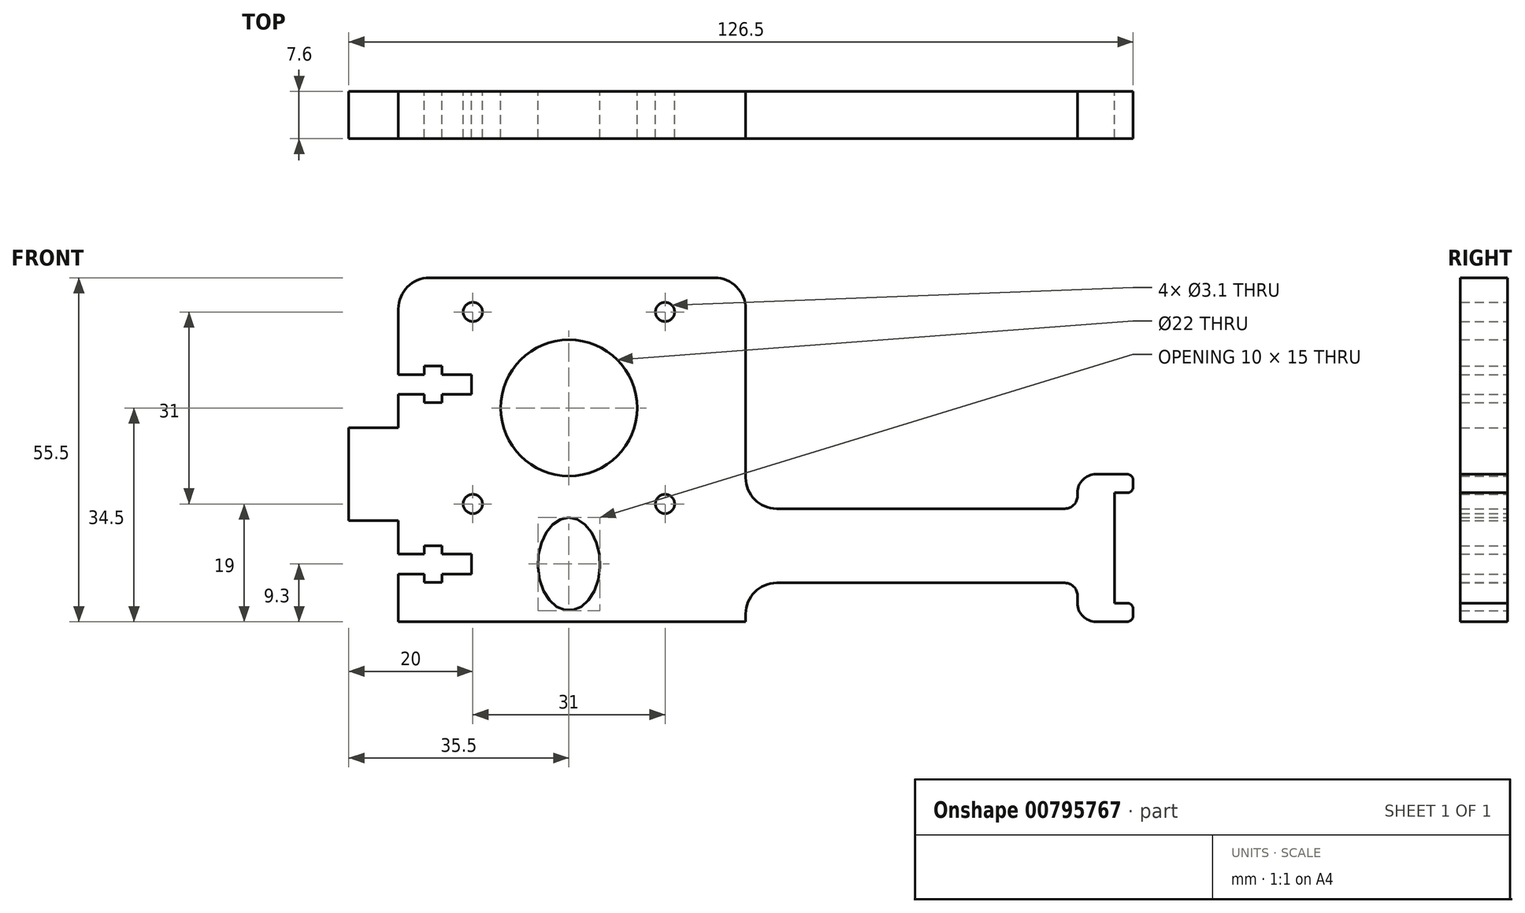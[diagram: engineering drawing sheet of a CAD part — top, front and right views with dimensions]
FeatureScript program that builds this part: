
annotation { "Feature Type Name" : "Feature", "Feature Type Description" : "" }
export const myFeature = defineFeature(function(context is Context, id is Id, definition is map)
    precondition{}
    {
        {
            var Q0;
            Q0=qCreatedBy(makeId("Front.planeOp"),FACE);
            var sketch = newSketch(context, id + "F0", { "sketchPlane" : qUnion([Q0])});
            skLineSegment(sketch, "E0", {"start": v(0, 0) * mm, "end": v(56, 0) * mm});
            skLineSegment(sketch, "E1", {"start": v(56, 0) * mm, "end": v(56, 1.25) * mm});
            skLineSegment(sketch, "E2", {"start": v(61, 6.25) * mm, "end": v(107.5, 6.25) * mm});
            skLineSegment(sketch, "E3", {"start": v(115.5, 3) * mm, "end": v(115.5, 20.8) * mm});
            skLineSegment(sketch, "E4", {"start": v(107.5, 18.25) * mm, "end": v(61, 18.25) * mm});
            skPoint(sketch, "E4.endSnap0", {"position": v(56, 3.12) * mm});
            skLineSegment(sketch, "E5", {"start": v(56, 23.25) * mm, "end": v(56, 50.5) * mm});
            skLineSegment(sketch, "E6", {"start": v(51, 55.5) * mm, "end": v(5, 55.5) * mm});
            skLineSegment(sketch, "E7", {"start": v(0, 50.5) * mm, "end": v(0, 39.9) * mm});
            skLineSegment(sketch, "E8", {"start": v(0, 31.3) * mm, "end": v(-8, 31.3) * mm});
            skLineSegment(sketch, "E9", {"start": v(-8, 31.3) * mm, "end": v(-8, 16.3) * mm});
            skLineSegment(sketch, "E10", {"start": v(-8, 16.3) * mm, "end": v(0, 16.3) * mm});
            skLineSegment(sketch, "E11", {"start": v(0, 16.3) * mm, "end": v(0, 10.9) * mm});
            skCircle(sketch, "E12", {"center": v(27.5, 34.5) * mm, "radius": 11 * mm});
            skCircle(sketch, "E13", {"center": v(43, 50) * mm, "radius": 1.55 * mm});
            skCircle(sketch, "E14.1.0", {"center": v(43, 19) * mm, "radius": 1.55 * mm});
            skCircle(sketch, "E14.2.0", {"center": v(12, 19) * mm, "radius": 1.55 * mm});
            skCircle(sketch, "E14.3.0", {"center": v(12, 50) * mm, "radius": 1.55 * mm});
            skLineSegment(sketch, "E14.anchor1", {"start": v(27.5, 34.5) * mm, "end": v(43, 50) * mm, "construction": true});
            skLineSegment(sketch, "E14.anchor2", {"start": v(27.5, 34.5) * mm, "end": v(12, 50) * mm, "construction": true});
            skLineSegment(sketch, "E15", {"start": v(0, 7.7) * mm, "end": v(4.2, 7.7) * mm});
            skLineSegment(sketch, "E16", {"start": v(4.2, 7.7) * mm, "end": v(4.2, 6.35) * mm});
            skLineSegment(sketch, "E17", {"start": v(7, 6.35) * mm, "end": v(7, 7.7) * mm});
            skLineSegment(sketch, "E18", {"start": v(7, 7.7) * mm, "end": v(11.8, 7.7) * mm});
            skLineSegment(sketch, "E19", {"start": v(11.8, 7.7) * mm, "end": v(11.8, 9.3) * mm});
            skLineSegment(sketch, "E20", {"start": v(7, 6.35) * mm, "end": v(4.2, 6.35) * mm});
            skLineSegment(sketch, "E21", {"start": v(0, 9.3) * mm, "end": v(11.8, 9.3) * mm, "construction": true});
            skLineSegment(sketch, "E22.MirrorCS", {"start": v(11.8, 10.9) * mm, "end": v(11.8, 9.3) * mm});
            skLineSegment(sketch, "E23.MirrorCS", {"start": v(7, 10.9) * mm, "end": v(11.8, 10.9) * mm});
            skLineSegment(sketch, "E24.MirrorCS", {"start": v(7, 12.25) * mm, "end": v(7, 10.9) * mm});
            skLineSegment(sketch, "E25.MirrorCS", {"start": v(7, 12.25) * mm, "end": v(4.2, 12.25) * mm});
            skLineSegment(sketch, "E26.MirrorCS", {"start": v(4.2, 10.9) * mm, "end": v(4.2, 12.25) * mm});
            skEllipse(sketch, "E27", {"center": v(27.5, 9.3) * mm, "majorRadius": 7.5 * mm, "minorRadius": 5 * mm, "majorAxis": v(0, 1)});
            skLineSegment(sketch, "E28", {"start": v(0, 53.5) * mm, "end": v(-8, 53.5) * mm, "construction": true});
            skLineSegment(sketch, "E29", {"start": v(0, 36.7) * mm, "end": v(4.2, 36.7) * mm});
            skLineSegment(sketch, "E30", {"start": v(4.2, 36.7) * mm, "end": v(4.2, 35.35) * mm});
            skLineSegment(sketch, "E31", {"start": v(7, 35.35) * mm, "end": v(7, 36.7) * mm});
            skLineSegment(sketch, "E32", {"start": v(7, 36.7) * mm, "end": v(11.8, 36.7) * mm});
            skLineSegment(sketch, "E33", {"start": v(11.8, 36.7) * mm, "end": v(11.8, 38.3) * mm});
            skLineSegment(sketch, "E34", {"start": v(7, 35.35) * mm, "end": v(4.2, 35.35) * mm});
            skLineSegment(sketch, "E35", {"start": v(0, 38.3) * mm, "end": v(11.8, 38.3) * mm, "construction": true});
            skLineSegment(sketch, "E36.MirrorCS", {"start": v(11.8, 39.9) * mm, "end": v(11.8, 38.3) * mm});
            skLineSegment(sketch, "E37.MirrorCS", {"start": v(7, 39.9) * mm, "end": v(11.8, 39.9) * mm});
            skLineSegment(sketch, "E38.MirrorCS", {"start": v(7, 41.25) * mm, "end": v(7, 39.9) * mm});
            skLineSegment(sketch, "E39.MirrorCS", {"start": v(7, 41.25) * mm, "end": v(4.2, 41.25) * mm});
            skLineSegment(sketch, "E40.MirrorCS", {"start": v(4.2, 39.9) * mm, "end": v(4.2, 41.25) * mm});
            skLineSegment(sketch, "E41", {"start": v(0, 3) * mm, "end": v(-8, 3) * mm, "construction": true});
            skLineSegment(sketch, "E42", {"start": v(-8, 31.3) * mm, "end": v(-8, 53.5) * mm, "construction": true});
            skLineSegment(sketch, "E43", {"start": v(-8, 16.3) * mm, "end": v(-8, 3) * mm, "construction": true});
            skLineSegment(sketch, "E44", {"start": v(-8, 3) * mm, "end": v(-8, 0) * mm, "construction": true});
            skLineSegment(sketch, "E45", {"start": v(-8, 0) * mm, "end": v(0, 0) * mm, "construction": true});
            skLineSegment(sketch, "E46", {"start": v(0, 36.7) * mm, "end": v(0, 31.3) * mm});
            skLineSegment(sketch, "E47", {"start": v(0, 7.7) * mm, "end": v(0, 0) * mm});
            skLineSegment(sketch, "E48", {"start": v(0, 39.9) * mm, "end": v(0, 36.7) * mm, "construction": true});
            skLineSegment(sketch, "E49", {"start": v(0, 10.9) * mm, "end": v(0, 7.7) * mm, "construction": true});
            skLineSegment(sketch, "E50.MirrorCS", {"start": v(0, 39.9) * mm, "end": v(4.2, 39.9) * mm});
            skLineSegment(sketch, "E51.MirrorCS", {"start": v(0, 10.9) * mm, "end": v(4.2, 10.9) * mm});
            skPoint(sketch, "E52.visualSharp", {"position": v(56, 55.5) * mm});
            skArc(sketch, "E52.filletArc", {"start": v(56, 50.5) * mm, "mid": v(54.54, 54.04) * mm, "end": v(51, 55.5) * mm});
            skPoint(sketch, "E53.visualSharp", {"position": v(0, 55.5) * mm});
            skArc(sketch, "E53.filletArc", {"start": v(5, 55.5) * mm, "mid": v(1.46, 54.04) * mm, "end": v(0, 50.5) * mm});
            skPoint(sketch, "E54.visualSharp", {"position": v(56, 18.25) * mm});
            skArc(sketch, "E54.filletArc", {"start": v(56, 23.25) * mm, "mid": v(57.46, 19.71) * mm, "end": v(61, 18.25) * mm});
            skPoint(sketch, "E55.visualSharp", {"position": v(56, 6.25) * mm});
            skArc(sketch, "E55.filletArc", {"start": v(61, 6.25) * mm, "mid": v(57.46, 4.79) * mm, "end": v(56, 1.25) * mm});
            skLineSegment(sketch, "E56", {"start": v(109.5, 4.25) * mm, "end": v(109.5, 3) * mm});
            skLineSegment(sketch, "E57", {"start": v(112.5, 0) * mm, "end": v(117.5, 0) * mm});
            skLineSegment(sketch, "E58", {"start": v(118.5, 1) * mm, "end": v(118.5, 2) * mm});
            skLineSegment(sketch, "E59", {"start": v(117.5, 3) * mm, "end": v(115.5, 3) * mm});
            skLineSegment(sketch, "E60", {"start": v(117.5, 20.8) * mm, "end": v(115.5, 20.8) * mm});
            skLineSegment(sketch, "E61", {"start": v(118.5, 21.8) * mm, "end": v(118.5, 22.8) * mm});
            skLineSegment(sketch, "E62", {"start": v(117.5, 23.8) * mm, "end": v(112.5, 23.8) * mm});
            skLineSegment(sketch, "E63", {"start": v(109.5, 20.8) * mm, "end": v(109.5, 20.25) * mm});
            skPoint(sketch, "E64.visualSharp", {"position": v(109.5, 23.8) * mm});
            skArc(sketch, "E64.filletArc", {"start": v(112.5, 23.8) * mm, "mid": v(110.38, 22.92) * mm, "end": v(109.5, 20.8) * mm});
            skPoint(sketch, "E65.visualSharp", {"position": v(109.5, 18.25) * mm});
            skArc(sketch, "E65.filletArc", {"start": v(107.5, 18.25) * mm, "mid": v(108.91, 18.84) * mm, "end": v(109.5, 20.25) * mm});
            skPoint(sketch, "E66.visualSharp", {"position": v(109.5, 6.25) * mm});
            skArc(sketch, "E66.filletArc", {"start": v(109.5, 4.25) * mm, "mid": v(108.91, 5.66) * mm, "end": v(107.5, 6.25) * mm});
            skPoint(sketch, "E67.visualSharp", {"position": v(109.5, 0) * mm});
            skArc(sketch, "E67.filletArc", {"start": v(109.5, 3) * mm, "mid": v(110.38, 0.88) * mm, "end": v(112.5, 0) * mm});
            skPoint(sketch, "E68.visualSharp", {"position": v(118.5, 23.8) * mm});
            skArc(sketch, "E68.filletArc", {"start": v(118.5, 22.8) * mm, "mid": v(118.2, 23.5) * mm, "end": v(117.5, 23.8) * mm});
            skPoint(sketch, "E69.visualSharp", {"position": v(118.5, 0) * mm});
            skArc(sketch, "E69.filletArc", {"start": v(117.5, 0) * mm, "mid": v(118.2, 0.3) * mm, "end": v(118.5, 1) * mm});
            skLineSegment(sketch, "E70", {"start": v(5.6, 41.25) * mm, "end": v(5.6, 35.35) * mm, "construction": true});
            skLineSegment(sketch, "E71", {"start": v(5.6, 12.25) * mm, "end": v(5.6, 6.35) * mm, "construction": true});
            skPoint(sketch, "E72.visualSharp", {"position": v(118.5, 20.8) * mm});
            skArc(sketch, "E72.filletArc", {"start": v(117.5, 20.8) * mm, "mid": v(118.2, 21.1) * mm, "end": v(118.5, 21.8) * mm});
            skPoint(sketch, "E73.visualSharp", {"position": v(118.5, 3) * mm});
            skArc(sketch, "E73.filletArc", {"start": v(118.5, 2) * mm, "mid": v(118.2, 2.7) * mm, "end": v(117.5, 3) * mm});
            skSolve(sketch);
        }
        {
            var Q0;
            Q0=makeQuery(id+"F0.imprint","IMPRINT",FACE,{"disambiguationData":[TD([[makeQuery(id+"F0.imprint","IMPRINT",EDGE,{"derivedFrom":sQuery(id+"F0.wireOp",EDGE,"E0")}),1.0]])]});
            extrude(context, id + "F1", {"entities" : qUnion([Q0]), "endBound" : BoundingType.SYMMETRIC, "depth" : 7.6 * mm, "offsetDistance" : 25 * mm});
        }
    });
